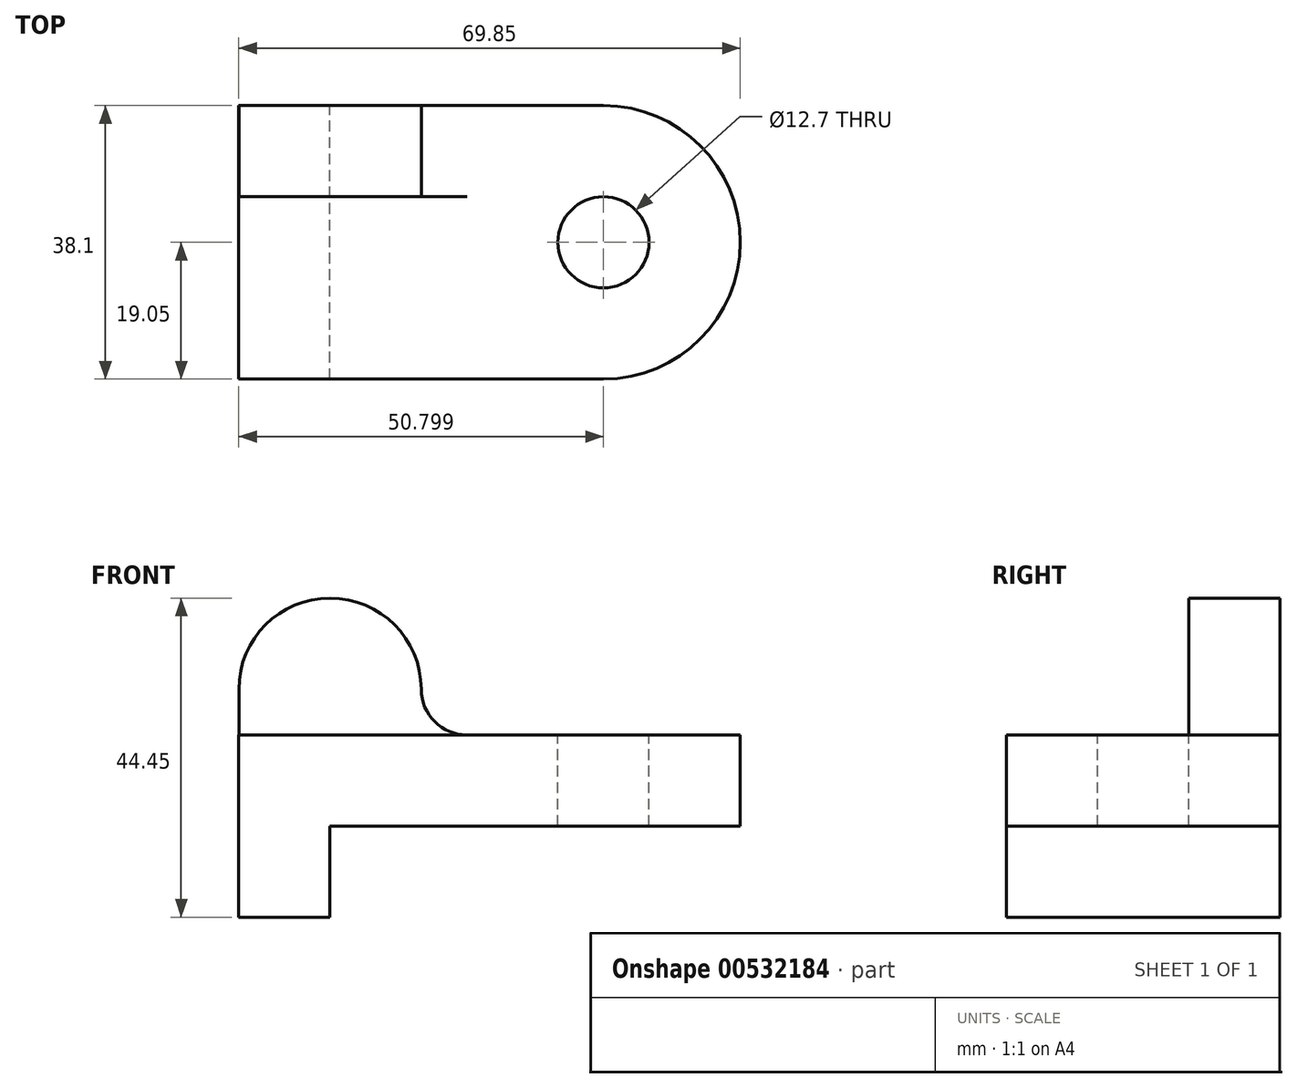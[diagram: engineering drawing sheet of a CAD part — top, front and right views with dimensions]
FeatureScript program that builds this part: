
annotation { "Feature Type Name" : "Feature", "Feature Type Description" : "" }
export const myFeature = defineFeature(function(context is Context, id is Id, definition is map)
    precondition{}
    {
        {
            var Q0;
            Q0=qCreatedBy(makeId("Top.planeOp"),FACE);
            var sketch = newSketch(context, id + "F0", { "sketchPlane" : qUnion([Q0])});
            skLineSegment(sketch, "E0", {"start": v(29.68, 0) * mm, "end": v(-21.12, 0) * mm});
            skLineSegment(sketch, "E1", {"start": v(-21.12, 0) * mm, "end": v(-21.12, -38.1) * mm});
            skLineSegment(sketch, "E2", {"start": v(-21.12, -38.1) * mm, "end": v(29.68, -38.1) * mm});
            skArc(sketch, "E3", {"start": v(29.68, 0) * mm, "mid": v(48.73, -19.05) * mm, "end": v(29.68, -38.1) * mm});
            skSolve(sketch);
        }
        {
            var Q0;
            Q0 = qSketchRegion(id + "F0", true);
            extrude(context, id + "F1", {"entities" : qUnion([Q0]), "depth" : 12.7 * mm, "offsetDistance" : 25.4 * mm});
        }
        {
            var Q0;
            Q0=qCreatedBy(makeId("Front.planeOp"),FACE);
            var sketch = newSketch(context, id + "F2", { "sketchPlane" : qUnion([Q0])});
            skLineSegment(sketch, "E4", {"start": v(-21.1, 0) * mm, "end": v(-21.1, 10.3) * mm, "construction": true});
            skLineSegment(sketch, "E5", {"start": v(-21.1, 10.3) * mm, "end": v(-21.1, 19.05) * mm});
            skLineSegment(sketch, "E6", {"start": v(19.42, 10.3) * mm, "end": v(-33.12, 10.3) * mm, "construction": true});
            skLineSegment(sketch, "E7", {"start": v(-21.1, 10.3) * mm, "end": v(4.3, 10.3) * mm});
            skLineSegment(sketch, "E8", {"start": v(4.3, 10.3) * mm, "end": v(4.3, 19.05) * mm});
            skArc(sketch, "E9", {"start": v(-21.1, 19.05) * mm, "mid": v(-8.4, 31.75) * mm, "end": v(4.3, 19.05) * mm});
            skSolve(sketch);
        }
        {
            var Q0;
            Q0 = qSketchRegion(id + "F2", true);
            extrude(context, id + "F3", {"entities" : qUnion([Q0]), "operationType" : NewBodyOperationType.ADD, "depth" : 12.7 * mm, "offsetDistance" : 25.4 * mm});
        }
        {
            var Q0;
            Q0=makeQuery(id+"F0.imprint","IMPRINT",FACE,{"disambiguationData":[TD([[makeQuery(id+"F0.imprint","IMPRINT",EDGE,{"derivedFrom":sQuery(id+"F0.wireOp",EDGE,"E0")}),1.0]])]});
            var sketch = newSketch(context, id + "F4", { "sketchPlane" : qUnion([Q0])});
            skLineSegment(sketch, "E10.bottom", {"start": v(-21.12, -38.1) * mm, "end": v(-8.42, -38.1) * mm});
            skLineSegment(sketch, "E10.top", {"start": v(-21.12, 0) * mm, "end": v(-8.42, 0) * mm});
            skLineSegment(sketch, "E10.left", {"start": v(-21.12, -38.1) * mm, "end": v(-21.12, 0) * mm});
            skLineSegment(sketch, "E10.right", {"start": v(-8.42, -38.1) * mm, "end": v(-8.42, 0) * mm});
            skSolve(sketch);
        }
        {
            var Q0;
            Q0 = qSketchRegion(id + "F4", true);
            extrude(context, id + "F5", {"entities" : qUnion([Q0]), "operationType" : NewBodyOperationType.ADD, "oppositeDirection" : true, "depth" : 12.7 * mm, "offsetDistance" : 25.4 * mm});
        }
        {
            var Q0;
            Q0=makeQuery(id+"F1.opExtrude","CAP_FACE",FACE,{"disambiguationData":[OSD([sQuery(id+"F0.wireOp",EDGE,"E0"),sQuery(id+"F0.wireOp",EDGE,"E1"),sQuery(id+"F0.wireOp",EDGE,"E2"),sQuery(id+"F0.wireOp",EDGE,"E3")])],"isStart":false});
            var sketch = newSketch(context, id + "F6", { "sketchPlane" : qUnion([Q0])});
            skCircle(sketch, "E11", {"center": v(29.68, -19.05) * mm, "radius": 6.35 * mm});
            skSolve(sketch);
        }
        {
            var Q0;
            Q0 = qSketchRegion(id + "F6", true);
            extrude(context, id + "F7", {"entities" : qUnion([Q0]), "operationType" : NewBodyOperationType.REMOVE, "oppositeDirection" : true, "depth" : 25.4 * mm, "offsetDistance" : 25.4 * mm});
        }
        {
            var Q0;
            Q0=makeQuery(id+"F3.boolean.opBoolean","INTERSECT",EDGE,{"derivedFrom":[makeQuery(id+"F1.opExtrude","CAP_FACE",FACE,{"disambiguationData":[OSD([sQuery(id+"F0.wireOp",EDGE,"E0"),sQuery(id+"F0.wireOp",EDGE,"E1"),sQuery(id+"F0.wireOp",EDGE,"E2"),sQuery(id+"F0.wireOp",EDGE,"E3")])],"isStart":false}),makeQuery(id+"F3.opExtrude","SWEPT_FACE",FACE,{"disambiguationData":[OSD([sQuery(id+"F2.wireOp",EDGE,"E8")])]})]});
            fillet(context, id + "F8", {"entities" : qUnion([Q0]), "radius" : 6.35 * mm, "tangentPropagation" : true, "allowEdgeOverflow" : false});
        }
    });
